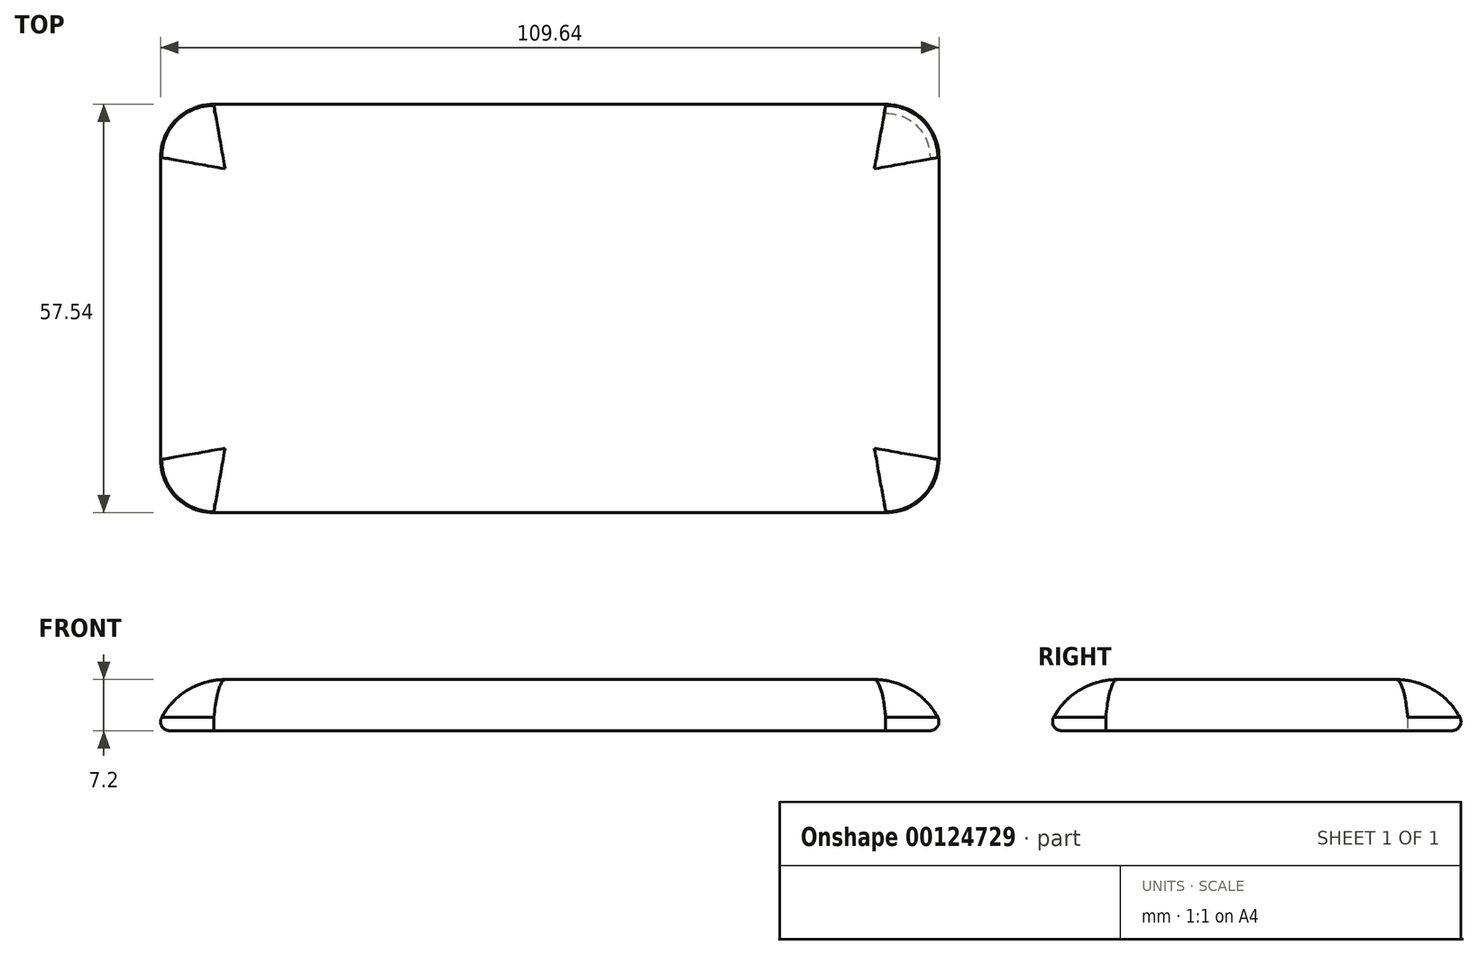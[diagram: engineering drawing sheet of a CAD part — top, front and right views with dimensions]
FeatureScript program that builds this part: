
annotation { "Feature Type Name" : "Feature", "Feature Type Description" : "" }
export const myFeature = defineFeature(function(context is Context, id is Id, definition is map)
    precondition{}
    {
        {
            var Q0;
            Q0=qCreatedBy(makeId("Top.planeOp"),FACE);
            var sketch = newSketch(context, id + "F0", { "sketchPlane" : qUnion([Q0])});
            skLineSegment(sketch, "E0.bottom", {"start": v(-55.45, 29.4) * mm, "end": v(55.45, 29.4) * mm});
            skLineSegment(sketch, "E0.top", {"start": v(-55.45, -29.4) * mm, "end": v(55.45, -29.4) * mm});
            skLineSegment(sketch, "E0.left", {"start": v(-55.45, 29.4) * mm, "end": v(-55.45, -29.4) * mm});
            skLineSegment(sketch, "E0.right", {"start": v(55.45, 29.4) * mm, "end": v(55.45, -29.4) * mm});
            skSolve(sketch);
        }
        {
            var Q0;
            Q0=qSketchRegion(id+"F0",true);
            extrude(context, id + "F1", {"entities" : qUnion([Q0]), "depth" : 7.2 * mm});
        }
        {
            var Q0;
            Q0=makeQuery(id+"F1.opExtrude","SWEPT_EDGE",EDGE,{"disambiguationData":[OSD([sQuery(id+"F0.wireOp",EDGE,"E0.top"),sQuery(id+"F0.wireOp",EDGE,"E0.left")])]});
            var Q1;
            Q1=makeQuery(id+"F1.opExtrude","SWEPT_EDGE",EDGE,{"disambiguationData":[OSD([sQuery(id+"F0.wireOp",EDGE,"E0.top"),sQuery(id+"F0.wireOp",EDGE,"E0.right")])]});
            var Q2;
            Q2=makeQuery(id+"F1.opExtrude","SWEPT_EDGE",EDGE,{"disambiguationData":[OSD([sQuery(id+"F0.wireOp",EDGE,"E0.bottom"),sQuery(id+"F0.wireOp",EDGE,"E0.left")])]});
            var Q3;
            Q3=makeQuery(id+"F1.opExtrude","SWEPT_EDGE",EDGE,{"disambiguationData":[OSD([sQuery(id+"F0.wireOp",EDGE,"E0.bottom"),sQuery(id+"F0.wireOp",EDGE,"E0.right")])]});
            fillet(context, id + "F2", {"entities" : qUnion([Q0, Q1, Q2, Q3]), "radius" : 8 * mm, "tangentPropagation" : true, "allowEdgeOverflow" : false});
        }
        {
            var Q0;
            Q0=makeQuery(id+"F1.opExtrude","CAP_FACE",FACE,{"disambiguationData":[OSD([sQuery(id+"F0.wireOp",EDGE,"E0.bottom"),sQuery(id+"F0.wireOp",EDGE,"E0.top"),sQuery(id+"F0.wireOp",EDGE,"E0.left"),sQuery(id+"F0.wireOp",EDGE,"E0.right")])],"isStart":false});
            fillet(context, id + "F3", {"entities" : qUnion([Q0]), "radius" : 10.16 * mm, "allowEdgeOverflow" : false});
        }
        {
            var Q0;
            Q0=makeQuery(id+"F1.opExtrude","CAP_FACE",FACE,{"disambiguationData":[OSD([sQuery(id+"F0.wireOp",EDGE,"E0.bottom"),sQuery(id+"F0.wireOp",EDGE,"E0.top"),sQuery(id+"F0.wireOp",EDGE,"E0.left"),sQuery(id+"F0.wireOp",EDGE,"E0.right")])],"isStart":true});
            fillet(context, id + "F4", {"entities" : qUnion([Q0]), "radius" : 1.27 * mm, "tangentPropagation" : true, "allowEdgeOverflow" : false});
        }
    });
